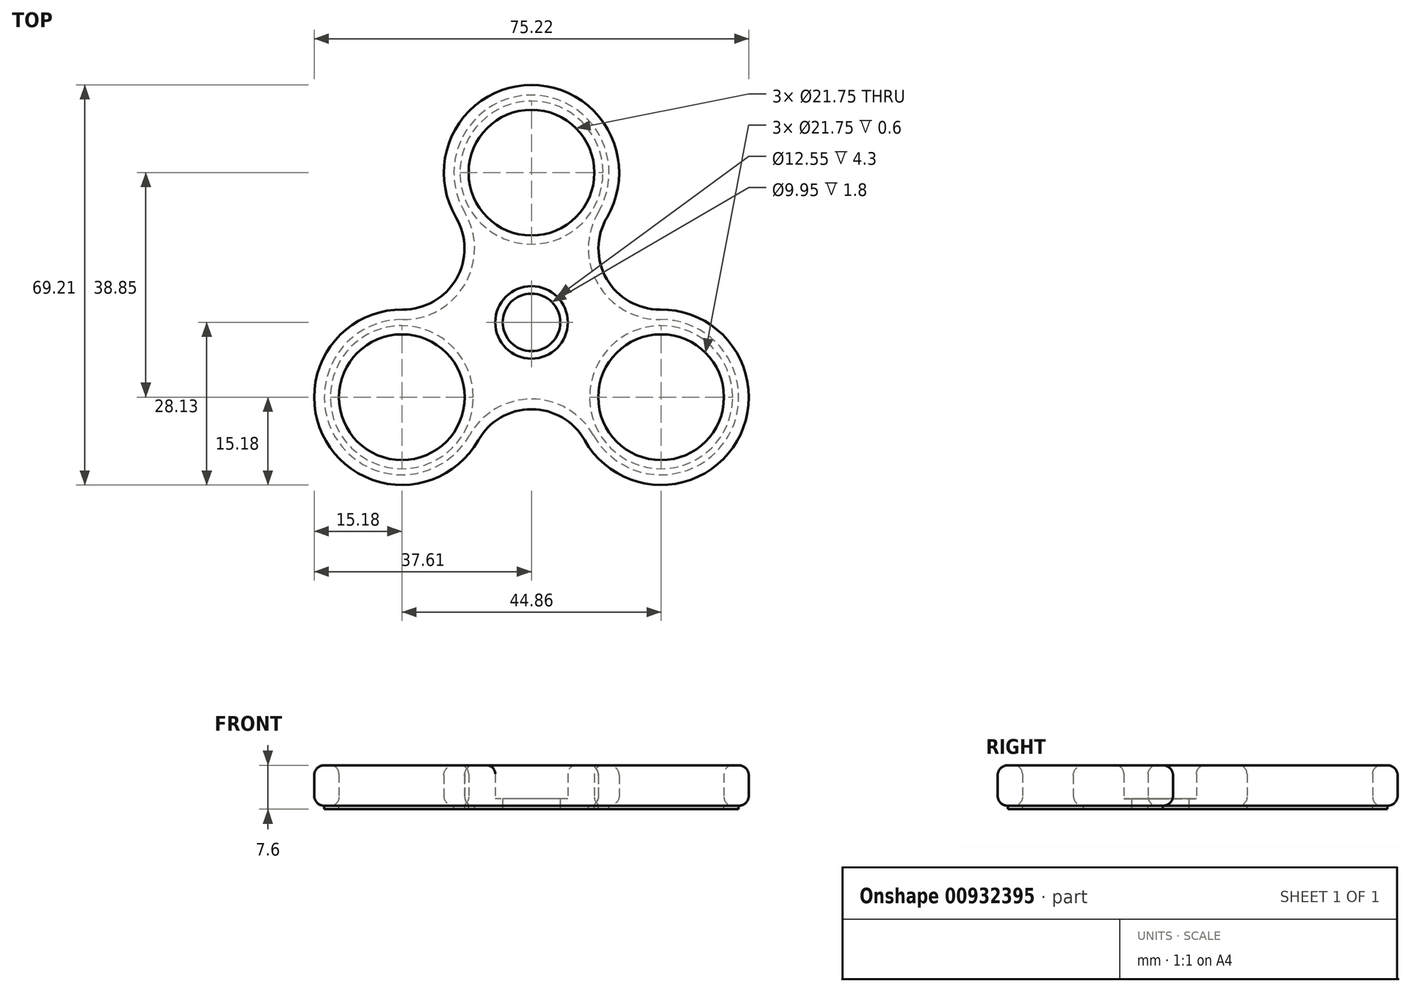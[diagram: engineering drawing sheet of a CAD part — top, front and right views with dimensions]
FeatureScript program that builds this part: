
annotation { "Feature Type Name" : "Feature", "Feature Type Description" : "" }
export const myFeature = defineFeature(function(context is Context, id is Id, definition is map)
    precondition{}
    {
        {
            var Q0;
            Q0=qCreatedBy(makeId("Top.planeOp"),FACE);
            var sketch = newSketch(context, id + "F0", { "sketchPlane" : qUnion([Q0])});
            skCircle(sketch, "E0", {"center": v(0, 0) * mm, "radius": 6.28 * mm});
            skCircle(sketch, "E1", {"center": v(0, 25.9) * mm, "radius": 10.88 * mm});
            skPoint(sketch, "E2", {"position": v(0, 15.03) * mm});
            skPoint(sketch, "E3", {"position": v(0, 6.28) * mm});
            skLineSegment(sketch, "E4", {"start": v(0, 15.03) * mm, "end": v(0, 6.27) * mm});
            skLineSegment(sketch, "E5", {"start": v(0, 0) * mm, "end": v(-13.01, 7.51) * mm});
            skPoint(sketch, "E6", {"position": v(-5.43, 3.14) * mm});
            skSolve(sketch);
        }
        {
            var Q0;
            Q0=qCreatedBy(makeId("Top.planeOp"),FACE);
            var sketch = newSketch(context, id + "F1", { "sketchPlane" : qUnion([Q0])});
            skArc(sketch, "E7", {"start": v(0, 41.08) * mm, "mid": v(-13.18, 33.42) * mm, "end": v(-13.07, 18.18) * mm});
            skArc(sketch, "E8", {"start": v(-13.01, 7.51) * mm, "mid": v(-11.6, 12.85) * mm, "end": v(-13.07, 18.18) * mm});
            skLineSegment(sketch, "E9", {"start": v(-13.01, 7.51) * mm, "end": v(-30.7, -23.13) * mm, "construction": true});
            skArc(sketch, "E10", {"start": v(0, 36.78) * mm, "mid": v(-10.88, 25.9) * mm, "end": v(0, 15.02) * mm});
            skLineSegment(sketch, "E11", {"start": v(0, 41.08) * mm, "end": v(0, 36.78) * mm, "construction": true});
            skLineSegment(sketch, "E12", {"start": v(0, 15.02) * mm, "end": v(0, 6.28) * mm, "construction": true});
            skLineSegment(sketch, "E13", {"start": v(-13.01, 7.51) * mm, "end": v(-5.43, 3.14) * mm});
            skLineSegment(sketch, "E14", {"start": v(0, 6.55) * mm, "end": v(0, 6.28) * mm});
            skArc(sketch, "E15", {"start": v(0, 6.28) * mm, "mid": v(-3.14, 5.43) * mm, "end": v(-5.43, 3.14) * mm});
            skArc(sketch, "E16.MirrorCS", {"start": v(0, 6.28) * mm, "mid": v(3.14, 5.43) * mm, "end": v(5.43, 3.14) * mm});
            skArc(sketch, "E17.MirrorCS", {"start": v(13.01, 7.51) * mm, "mid": v(11.6, 12.85) * mm, "end": v(13.07, 18.18) * mm});
            skArc(sketch, "E18.MirrorCS", {"start": v(0, 36.78) * mm, "mid": v(10.88, 25.9) * mm, "end": v(0, 15.02) * mm});
            skArc(sketch, "E19.MirrorCS", {"start": v(0, 41.08) * mm, "mid": v(13.18, 33.42) * mm, "end": v(13.07, 18.18) * mm});
            skLineSegment(sketch, "E20", {"start": v(5.43, 3.14) * mm, "end": v(13.01, 7.51) * mm});
            skSolve(sketch);
        }
        {
            var Q0;
            Q0 = qSketchRegion(id + "F1", true);
            extrude(context, id + "F2", {"entities" : qUnion([Q0]), "depth" : 7 * mm, "offsetDistance" : 25 * mm});
        }
        {
            var Q0;
            Q0=qCreatedBy(makeId("Right.planeOp"),FACE);
            var sketch = newSketch(context, id + "F3", { "sketchPlane" : qUnion([Q0])});
            skLineSegment(sketch, "E21", {"start": v(0, 0) * mm, "end": v(0, -42.25) * mm});
            skSolve(sketch);
        }
        {
            var Q0;
            Q0=makeQuery(id+"F2.opExtrude","SWEPT_BODY",BODY,{"disambiguationData":[OSD([sQuery(id+"F1.wireOp",EDGE,"E7"),sQuery(id+"F1.wireOp",EDGE,"E8"),sQuery(id+"F1.wireOp",EDGE,"E10"),sQuery(id+"F1.wireOp",EDGE,"E13"),sQuery(id+"F1.wireOp",EDGE,"E15"),sQuery(id+"F1.wireOp",EDGE,"E16.MirrorCS"),sQuery(id+"F1.wireOp",EDGE,"E17.MirrorCS"),sQuery(id+"F1.wireOp",EDGE,"E18.MirrorCS"),sQuery(id+"F1.wireOp",EDGE,"E19.MirrorCS"),sQuery(id+"F1.wireOp",EDGE,"E20")])]});
            var Q1;
            Q1=sQuery(id+"F3.wireOp",EDGE,"E21");
            circularPattern(context, id + "F4", {"operationType" : NewBodyOperationType.ADD, "entities" : qUnion([Q0]), "axis" : qUnion([Q1]), "angle" : 360 * degree, "instanceCount" : 3, "equalSpace" : true});
        }
        {
            var Q0;
            Q0=qCreatedBy(makeId("Top.planeOp"),FACE);
            var sketch = newSketch(context, id + "F5", { "sketchPlane" : qUnion([Q0])});
            skCircle(sketch, "E22", {"center": v(0, 0) * mm, "radius": 4.98 * mm});
            skCircle(sketch, "E23.0", {"center": v(0, 0) * mm, "radius": 6.28 * mm});
            skSolve(sketch);
        }
        {
            var Q0;
            Q0 = qSketchRegion(id + "F5", true);
            extrude(context, id + "F6", {"entities" : qUnion([Q0]), "operationType" : NewBodyOperationType.ADD, "depth" : 1.2 * mm, "offsetDistance" : 25 * mm});
        }
        {
            var Q0;
            Q0=makeQuery(id+"F4.opPattern","COPY",EDGE,{"derivedFrom":makeQuery(id+"F2.opExtrude","CAP_EDGE",EDGE,{"disambiguationData":[OSD([sQuery(id+"F1.wireOp",EDGE,"E7"),sQuery(id+"F1.wireOp",EDGE,"E19.MirrorCS")])],"isStart":true}),"instanceName":"2"});
            fillet(context, id + "F7", {"entities" : qUnion([Q0]), "radius" : 1.75 * mm, "tangentPropagation" : true, "allowEdgeOverflow" : false});
        }
        {
            var Q0;
            Q0=makeQuery(id+"F4.opPattern","COPY",EDGE,{"derivedFrom":makeQuery(id+"F2.opExtrude","CAP_EDGE",EDGE,{"disambiguationData":[OSD([sQuery(id+"F1.wireOp",EDGE,"E7"),sQuery(id+"F1.wireOp",EDGE,"E19.MirrorCS")])],"isStart":false}),"instanceName":"2"});
            fillet(context, id + "F8", {"entities" : qUnion([Q0]), "radius" : 1.75 * mm, "tangentPropagation" : true, "allowEdgeOverflow" : false});
        }
        {
            var Q0;
            Q0=makeQuery(id+"F4.opPattern","COPY",EDGE,{"derivedFrom":makeQuery(id+"F2.opExtrude","CAP_EDGE",EDGE,{"disambiguationData":[OSD([sQuery(id+"F1.wireOp",EDGE,"E10"),sQuery(id+"F1.wireOp",EDGE,"E18.MirrorCS")])],"isStart":false}),"instanceName":"2"});
            var Q1;
            Q1=makeQuery(id+"F2.opExtrude","CAP_EDGE",EDGE,{"disambiguationData":[OSD([sQuery(id+"F1.wireOp",EDGE,"E10"),sQuery(id+"F1.wireOp",EDGE,"E18.MirrorCS")])],"isStart":false});
            var Q2;
            Q2=makeQuery(id+"F4.opPattern","COPY",EDGE,{"derivedFrom":makeQuery(id+"F2.opExtrude","CAP_EDGE",EDGE,{"disambiguationData":[OSD([sQuery(id+"F1.wireOp",EDGE,"E10"),sQuery(id+"F1.wireOp",EDGE,"E18.MirrorCS")])],"isStart":false}),"instanceName":"1"});
            var Q3;
            Q3=makeQuery(id+"F4.opPattern","COPY",EDGE,{"derivedFrom":makeQuery(id+"F2.opExtrude","CAP_EDGE",EDGE,{"disambiguationData":[OSD([sQuery(id+"F1.wireOp",EDGE,"E10"),sQuery(id+"F1.wireOp",EDGE,"E18.MirrorCS")])],"isStart":true}),"instanceName":"2"});
            var Q4;
            Q4=makeQuery(id+"F4.opPattern","COPY",EDGE,{"derivedFrom":makeQuery(id+"F2.opExtrude","CAP_EDGE",EDGE,{"disambiguationData":[OSD([sQuery(id+"F1.wireOp",EDGE,"E10"),sQuery(id+"F1.wireOp",EDGE,"E18.MirrorCS")])],"isStart":true}),"instanceName":"1"});
            var Q5;
            Q5=makeQuery(id+"F2.opExtrude","CAP_EDGE",EDGE,{"disambiguationData":[OSD([sQuery(id+"F1.wireOp",EDGE,"E10"),sQuery(id+"F1.wireOp",EDGE,"E18.MirrorCS")])],"isStart":true});
            var Q6;
            {var subQ0=makeQuery(id+"F2.opExtrude","CAP_EDGE",EDGE,{"disambiguationData":[OSD([sQuery(id+"F1.wireOp",EDGE,"E15"),sQuery(id+"F1.wireOp",EDGE,"E16.MirrorCS")])],"isStart":false});Q6=makeQuery(id+"F4.boolean.opBoolean","MERGE",EDGE,{"derivedFrom":[subQ0,makeQuery(id+"F4.opPattern","COPY",EDGE,{"derivedFrom":subQ0,"instanceName":"1"}),makeQuery(id+"F4.opPattern","COPY",EDGE,{"derivedFrom":subQ0,"instanceName":"2"})]});}
            fillet(context, id + "F9", {"entities" : qUnion([Q0, Q1, Q2, Q3, Q4, Q5, Q6]), "radius" : 1.5 * mm, "tangentPropagation" : true, "allowEdgeOverflow" : false});
        }
        {
            var Q0;
            Q0=qCreatedBy(makeId("Top.planeOp"),FACE);
            var sketch = newSketch(context, id + "F10", { "sketchPlane" : qUnion([Q0])});
            skArc(sketch, "E24.0.0", {"start": v(-11.56, 19.07) * mm, "mid": v(0, 39.32) * mm, "end": v(11.56, 19.07) * mm});
            skArc(sketch, "E24.0.1", {"start": v(11.56, 19.07) * mm, "mid": v(11.5, 6.64) * mm, "end": v(22.3, 0.47) * mm});
            skArc(sketch, "E24.0.2", {"start": v(22.3, 0.47) * mm, "mid": v(34.06, -19.66) * mm, "end": v(10.74, -19.55) * mm});
            skArc(sketch, "E24.0.3", {"start": v(10.74, -19.55) * mm, "mid": v(0, -13.27) * mm, "end": v(-10.74, -19.55) * mm});
            skArc(sketch, "E24.0.4", {"start": v(-10.74, -19.55) * mm, "mid": v(-34.06, -19.66) * mm, "end": v(-22.3, 0.47) * mm});
            skArc(sketch, "E24.0.5", {"start": v(-22.3, 0.47) * mm, "mid": v(-11.5, 6.64) * mm, "end": v(-11.56, 19.07) * mm});
            skCircle(sketch, "E25.0", {"center": v(22.43, -12.95) * mm, "radius": 10.88 * mm});
            skCircle(sketch, "E25.1", {"center": v(0, 25.9) * mm, "radius": 10.88 * mm});
            skCircle(sketch, "E25.2", {"center": v(-22.43, -12.95) * mm, "radius": 10.88 * mm});
            skCircle(sketch, "E26.0", {"center": v(0, 0) * mm, "radius": 4.98 * mm});
            skSolve(sketch);
        }
        {
            var Q0;
            Q0 = qSketchRegion(id + "F10", true);
            extrude(context, id + "F11", {"entities" : qUnion([Q0]), "operationType" : NewBodyOperationType.ADD, "oppositeDirection" : true, "depth" : .6 * mm, "offsetDistance" : 25 * mm});
        }
    });
